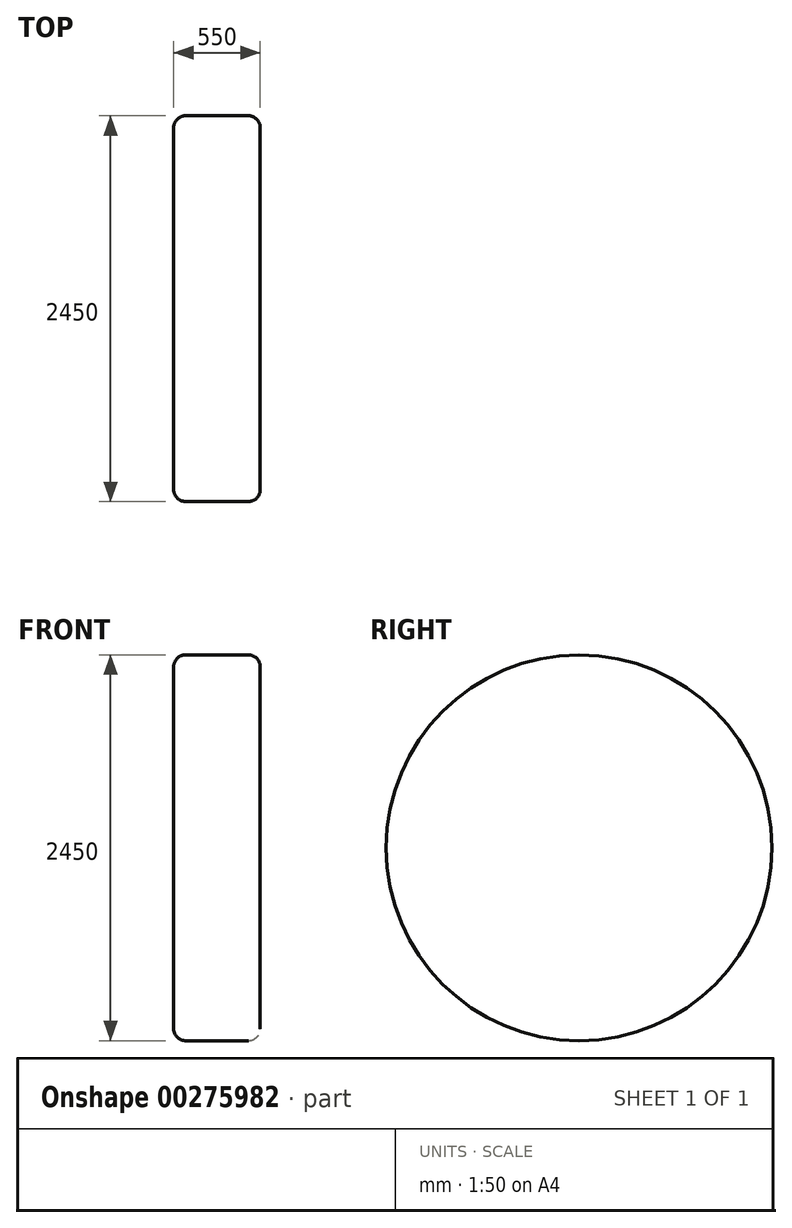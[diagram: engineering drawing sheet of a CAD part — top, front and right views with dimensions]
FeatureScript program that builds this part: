
annotation { "Feature Type Name" : "Feature", "Feature Type Description" : "" }
export const myFeature = defineFeature(function(context is Context, id is Id, definition is map)
    precondition{}
    {
        {
            var Q0;
            Q0=qCreatedBy(makeId("Front.planeOp"),FACE);
            var sketch = newSketch(context, id + "F0", { "sketchPlane" : qUnion([Q0])});
            skCircle(sketch, "E0", {"center": v(0, 0) * mm, "radius": 1225 * mm});
            skSolve(sketch);
        }
        {
            var Q0;
            Q0=makeQuery(id+"F0.imprint","IMPRINT",FACE,{"disambiguationData":[TD([[makeQuery(id+"F0.imprint","IMPRINT",EDGE,{"derivedFrom":sQuery(id+"F0.wireOp",EDGE,"E0")}),1.0]])]});
            extrude(context, id + "F1", {"entities" : qUnion([Q0]), "depth" : 550 * mm, "symmetric" : true});
        }
        {
            var Q0;
            Q0=makeQuery(id+"F1.opExtrude","CAP_EDGE",EDGE,{"disambiguationData":[OSD([sQuery(id+"F0.wireOp",EDGE,"E0")])],"isStart":false});
            var Q1;
            Q1=makeQuery(id+"F1.opExtrude","CAP_EDGE",EDGE,{"disambiguationData":[OSD([sQuery(id+"F0.wireOp",EDGE,"E0")])],"isStart":true});
            fillet(context, id + "F2", {"entities" : qUnion([Q0, Q1]), "radius" : 75 * mm, "tangentPropagation" : true, "allowEdgeOverflow" : false});
        }
        {
            var Q0;
            Q0=qCreatedBy(makeId("Right.planeOp"),FACE);
            var sketch = newSketch(context, id + "F3", { "sketchPlane" : qUnion([Q0])});
            skLineSegment(sketch, "E1", {"start": v(0, 0) * mm, "end": v(0, 766.95) * mm});
            skSolve(sketch);
        }
        {
            var Q0;
            Q0=makeQuery(id+"F1.opExtrude","SWEPT_BODY",BODY,{"disambiguationData":[OSD([sQuery(id+"F0.wireOp",EDGE,"E0")])]});
            var Q1;
            Q1=sQuery(id+"F3.wireOp",EDGE,"E1");
            transform(context, id + "F4", {"entities" : qUnion([Q0]), "transformType" : TransformType.ROTATION, "transformAxis" : qUnion([Q1]), "angle" : 90 * degree, "makeCopy" : false});
        }
    });
